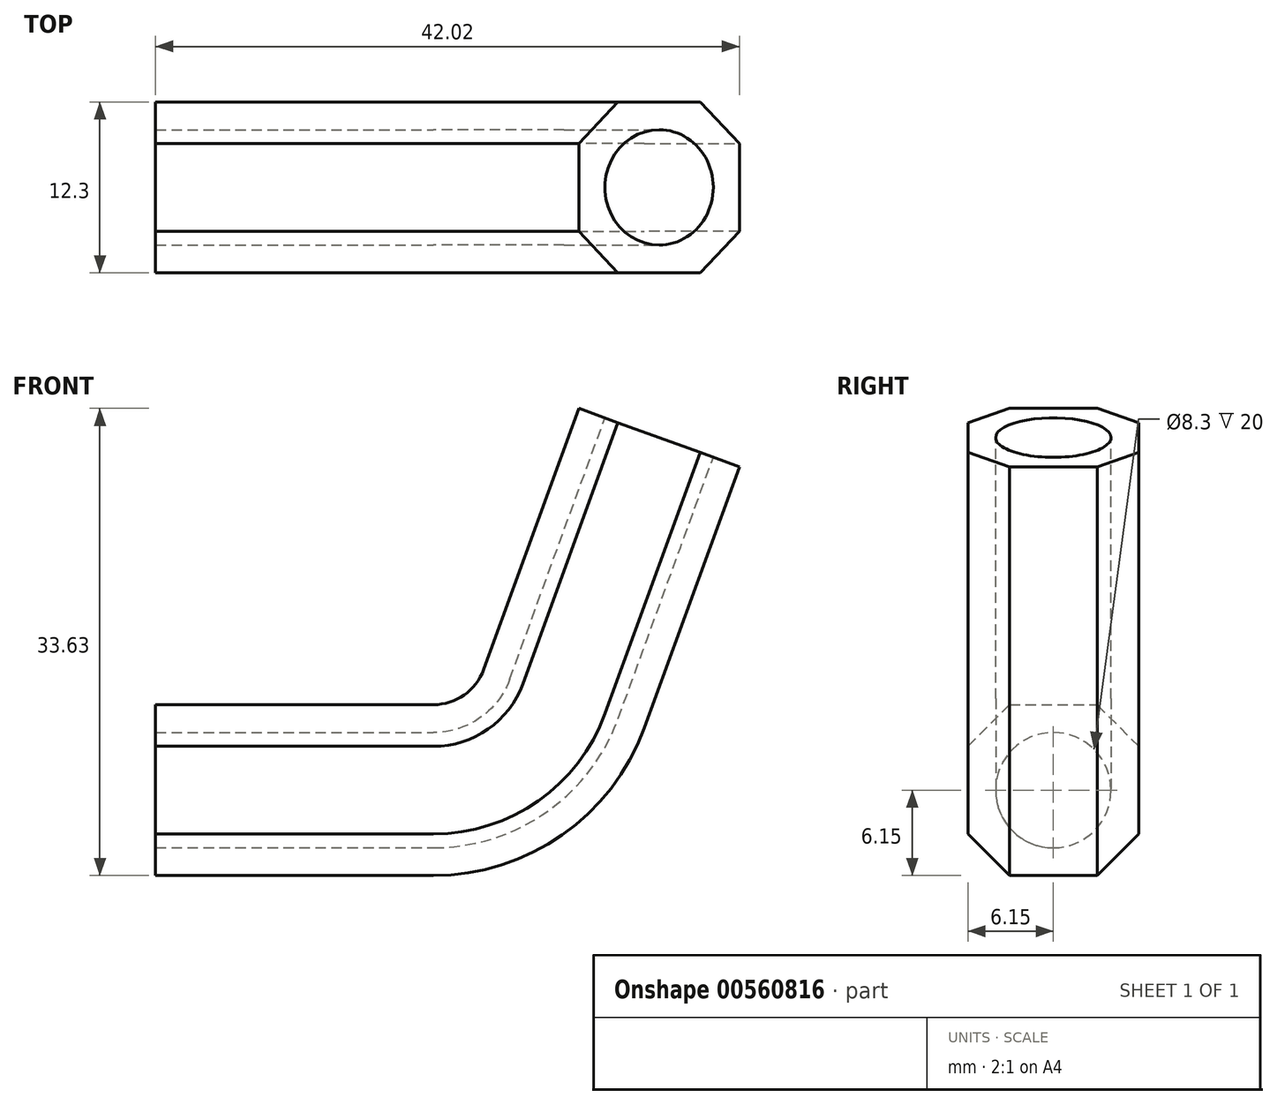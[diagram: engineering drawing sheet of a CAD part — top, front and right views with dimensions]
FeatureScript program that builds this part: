
annotation { "Feature Type Name" : "Feature", "Feature Type Description" : "" }
export const myFeature = defineFeature(function(context is Context, id is Id, definition is map)
    precondition{}
    {
        {
            var Q0;
            Q0=qCreatedBy(makeId("Front.planeOp"),FACE);
            var sketch = newSketch(context, id + "F0", { "sketchPlane" : qUnion([Q0])});
            skLineSegment(sketch, "E0", {"start": v(0, 0) * mm, "end": v(20, 0) * mm});
            skLineSegment(sketch, "E1", {"start": v(29.4, 6.58) * mm, "end": v(36.24, 25.37) * mm});
            skPoint(sketch, "E2.visualSharp", {"position": v(27, 0) * mm});
            skArc(sketch, "E2.filletArc", {"start": v(20, 0) * mm, "mid": v(25.74, 1.8) * mm, "end": v(29.4, 6.58) * mm});
            skLineSegment(sketch, "E3", {"start": v(27, 0) * mm, "end": v(-73, 0) * mm, "construction": true});
            skLineSegment(sketch, "E4", {"start": v(-73, 0) * mm, "end": v(-73, 401.75) * mm, "construction": true});
            skLineSegment(sketch, "E5", {"start": v(-73, 401.75) * mm, "end": v(173.23, 401.75) * mm, "construction": true});
            skLineSegment(sketch, "E6", {"start": v(173.23, 401.75) * mm, "end": v(27, 0) * mm, "construction": true});
            skSolve(sketch);
        }
        {
            var Q0;
            Q0=qCreatedBy(makeId("Right.planeOp"),FACE);
            var sketch = newSketch(context, id + "F1", { "sketchPlane" : qUnion([Q0])});
            skCircle(sketch, "E7", {"center": v(0, 0) * mm, "radius": 4.15 * mm});
            skCircle(sketch, "E8", {"center": v(0, 0) * mm, "radius": 6.15 * mm, "construction": true});
            skLineSegment(sketch, "E9.bottom", {"start": v(-6.15, 6.15) * mm, "end": v(6.15, 6.15) * mm});
            skLineSegment(sketch, "E9.top", {"start": v(-6.15, -6.15) * mm, "end": v(6.15, -6.15) * mm});
            skLineSegment(sketch, "E9.left", {"start": v(-6.15, 6.15) * mm, "end": v(-6.15, -6.15) * mm});
            skLineSegment(sketch, "E9.right", {"start": v(6.15, 6.15) * mm, "end": v(6.15, -6.15) * mm});
            skSolve(sketch);
        }
        {
            var Q0;
            Q0=makeQuery(id+"F1.imprint","IMPRINT",FACE,{"disambiguationData":[TD([[makeQuery(id+"F1.imprint","IMPRINT",EDGE,{"derivedFrom":sQuery(id+"F1.wireOp",EDGE,"E7")}),-1.0]])]});
            var Q1;
            Q1=sQuery(id+"F0.wireOp",EDGE,"E0");
            var Q2;
            Q2=sQuery(id+"F0.wireOp",EDGE,"E2.filletArc");
            var Q3;
            Q3=sQuery(id+"F0.wireOp",EDGE,"E1");
            sweep(context, id + "F2", {"profiles" : qUnion([Q0]), "path" : qUnion([Q1, Q2, Q3])});
        }
        {
            var Q0;
            Q0=makeQuery(id+"F2.opSweep","SWEPT_EDGE",EDGE,{"disambiguationData":[OSD([sQuery(id+"F0.wireOp",EDGE,"E1"),sQuery(id+"F1.wireOp",EDGE,"E9.bottom"),sQuery(id+"F1.wireOp",EDGE,"E9.left")])]});
            var Q1;
            Q1=makeQuery(id+"F2.opSweep","SWEPT_EDGE",EDGE,{"disambiguationData":[OSD([sQuery(id+"F0.wireOp",EDGE,"E1"),sQuery(id+"F1.wireOp",EDGE,"E9.top"),sQuery(id+"F1.wireOp",EDGE,"E9.left")])]});
            var Q2;
            Q2=makeQuery(id+"F2.opSweep","SWEPT_EDGE",EDGE,{"disambiguationData":[OSD([sQuery(id+"F0.wireOp",EDGE,"E1"),sQuery(id+"F1.wireOp",EDGE,"E9.top"),sQuery(id+"F1.wireOp",EDGE,"E9.right")])]});
            var Q3;
            Q3=makeQuery(id+"F2.opSweep","SWEPT_EDGE",EDGE,{"disambiguationData":[OSD([sQuery(id+"F0.wireOp",EDGE,"E1"),sQuery(id+"F1.wireOp",EDGE,"E9.bottom"),sQuery(id+"F1.wireOp",EDGE,"E9.right")])]});
            chamfer(context, id + "F3", {"entities" : qUnion([Q0, Q1, Q2, Q3]), "width" : 3 * mm, "tangentPropagation" : true});
        }
    });
